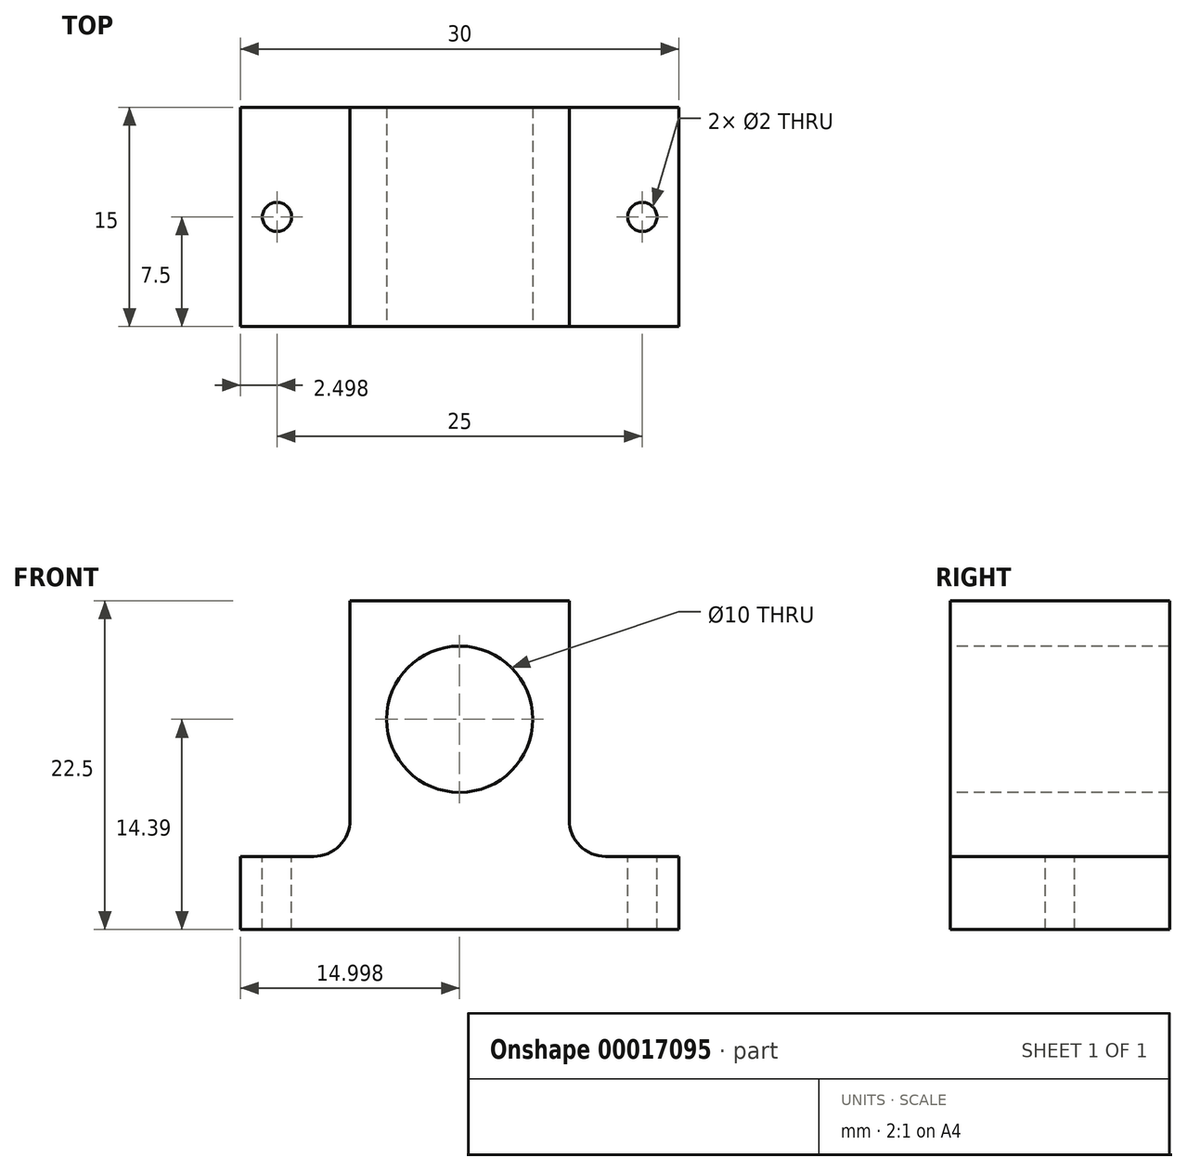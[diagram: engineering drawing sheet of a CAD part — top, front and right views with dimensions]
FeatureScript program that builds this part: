
annotation { "Feature Type Name" : "Feature", "Feature Type Description" : "" }
export const myFeature = defineFeature(function(context is Context, id is Id, definition is map)
    precondition{}
    {
        {
            var Q0;
            Q0=qCreatedBy(makeId("Front.planeOp"),FACE);
            var sketch = newSketch(context, id + "F0", { "sketchPlane" : qUnion([Q0])});
            skLineSegment(sketch, "E0", {"start": v(-17.56, 2.7) * mm, "end": v(-2.56, 2.7) * mm});
            skLineSegment(sketch, "E1", {"start": v(-2.56, 2.7) * mm, "end": v(-2.56, -12.3) * mm});
            skLineSegment(sketch, "E2", {"start": v(-0.06, -14.8) * mm, "end": v(4.94, -14.8) * mm});
            skLineSegment(sketch, "E3", {"start": v(4.94, -14.8) * mm, "end": v(4.94, -19.8) * mm});
            skLineSegment(sketch, "E4", {"start": v(4.94, -19.8) * mm, "end": v(-25.06, -19.8) * mm});
            skLineSegment(sketch, "E5", {"start": v(-25.06, -19.8) * mm, "end": v(-25.06, -14.8) * mm});
            skLineSegment(sketch, "E6", {"start": v(-25.06, -14.8) * mm, "end": v(-20.06, -14.8) * mm});
            skLineSegment(sketch, "E7", {"start": v(-17.56, -12.3) * mm, "end": v(-17.56, 2.7) * mm});
            skPoint(sketch, "E8.visualSharp", {"position": v(-17.56, -14.8) * mm});
            skArc(sketch, "E8.filletArc", {"start": v(-20.06, -14.8) * mm, "mid": v(-18.3, -14.06) * mm, "end": v(-17.56, -12.3) * mm});
            skPoint(sketch, "E9.visualSharp", {"position": v(-2.56, -14.8) * mm});
            skArc(sketch, "E9.filletArc", {"start": v(-2.56, -12.3) * mm, "mid": v(-1.83, -14.06) * mm, "end": v(-0.06, -14.8) * mm});
            skSolve(sketch);
        }
        {
            var Q0;
            Q0=makeQuery(id+"F0.imprint","IMPRINT",FACE,{"disambiguationData":[TD([[makeQuery(id+"F0.imprint","IMPRINT",EDGE,{"derivedFrom":sQuery(id+"F0.wireOp",EDGE,"E0")}),-1.0]])]});
            extrude(context, id + "F1", {"entities" : qUnion([Q0]), "depth" : 15 * mm});
        }
        {
            var Q0;
            Q0=makeQuery(id+"F1.opExtrude","SWEPT_FACE",FACE,{"disambiguationData":[OSD([sQuery(id+"F0.wireOp",EDGE,"E2")])]});
            var sketch = newSketch(context, id + "F2", { "sketchPlane" : qUnion([Q0])});
            skCircle(sketch, "E10", {"center": v(2.44, -7.5) * mm, "radius": 1 * mm});
            skSolve(sketch);
        }
        {
            var Q0;
            Q0 = qSketchRegion(id + "F2", true);
            var Q1;
            Q1=makeQuery(id+"F2.imprint","IMPRINT",FACE,{"disambiguationData":[TD([[makeQuery(id+"F2.imprint","IMPRINT",EDGE,{"derivedFrom":sQuery(id+"F2.wireOp",EDGE,"E10")}),1.0]])]});
            extrude(context, id + "F3", {"entities" : qUnion([Q0, Q1]), "operationType" : NewBodyOperationType.REMOVE, "endBound" : BoundingType.THROUGH_ALL, "oppositeDirection" : true, "depth" : 25 * mm});
        }
        {
            var Q0;
            Q0=makeQuery(id+"F1.opExtrude","SWEPT_FACE",FACE,{"disambiguationData":[OSD([sQuery(id+"F0.wireOp",EDGE,"E6")])]});
            var sketch = newSketch(context, id + "F4", { "sketchPlane" : qUnion([Q0])});
            skCircle(sketch, "E11", {"center": v(-22.56, -7.5) * mm, "radius": 1 * mm});
            skSolve(sketch);
        }
        {
            var Q0;
            Q0=makeQuery(id+"F4.imprint","IMPRINT",FACE,{"disambiguationData":[TD([[makeQuery(id+"F4.imprint","IMPRINT",EDGE,{"derivedFrom":sQuery(id+"F4.wireOp",EDGE,"E11")}),1.0]])]});
            extrude(context, id + "F5", {"entities" : qUnion([Q0]), "operationType" : NewBodyOperationType.REMOVE, "oppositeDirection" : true, "depth" : 25 * mm});
        }
        {
            var Q0;
            Q0=makeQuery(id+"F1.opExtrude","CAP_FACE",FACE,{"disambiguationData":[OSD([sQuery(id+"F0.wireOp",EDGE,"E0"),sQuery(id+"F0.wireOp",EDGE,"E1"),sQuery(id+"F0.wireOp",EDGE,"E2"),sQuery(id+"F0.wireOp",EDGE,"E3"),sQuery(id+"F0.wireOp",EDGE,"E4"),sQuery(id+"F0.wireOp",EDGE,"E5"),sQuery(id+"F0.wireOp",EDGE,"E6"),sQuery(id+"F0.wireOp",EDGE,"E7"),sQuery(id+"F0.wireOp",EDGE,"E8.filletArc"),sQuery(id+"F0.wireOp",EDGE,"E9.filletArc")])],"isStart":false});
            var sketch = newSketch(context, id + "F6", { "sketchPlane" : qUnion([Q0])});
            skCircle(sketch, "E12", {"center": v(-10.06, -5.41) * mm, "radius": 5 * mm});
            skSolve(sketch);
        }
        {
            var Q0;
            Q0=makeQuery(id+"F6.imprint","IMPRINT",FACE,{"disambiguationData":[TD([[makeQuery(id+"F6.imprint","IMPRINT",EDGE,{"derivedFrom":sQuery(id+"F6.wireOp",EDGE,"E12")}),1.0]])]});
            extrude(context, id + "F7", {"entities" : qUnion([Q0]), "operationType" : NewBodyOperationType.REMOVE, "endBound" : BoundingType.THROUGH_ALL, "oppositeDirection" : true, "depth" : 25 * mm});
        }
    });
